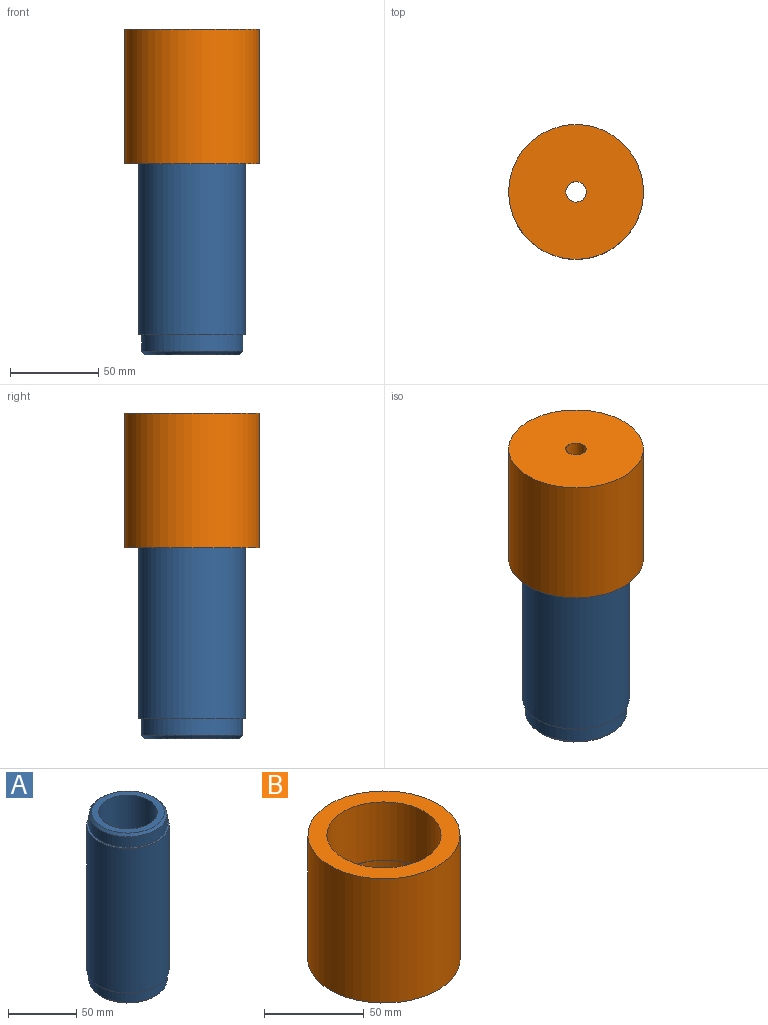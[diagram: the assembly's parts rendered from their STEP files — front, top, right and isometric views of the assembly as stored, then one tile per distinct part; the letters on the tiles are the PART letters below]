
ASSEMBLY  parts=2 mates=1
PART A: 10 faces, bbox 60.3x60.3x152.4 mm
  f0: cylinder r=30.16mm len=129.54mm, axis (0,0,-1), area 24550mm2, adj f1,f9
  f1: plane 60.33x60.33mm, normal (0,0,-1), area 292.9mm2, adj f0,f2
  f2: cylinder r=28.57mm len=57.15mm, axis (0,0,-1), area 1710.1mm2, adj f1,f3
  f3: cone r=28.57mm half-angle=45deg, axis (0,0,1), area 467.6mm2, adj f2,f4
  f4: plane 53.34x53.34mm, normal (0,0,-1), area 792.5mm2, adj f3,f5
  f5: cylinder r=21.42mm len=152.4mm, axis (0,0,-1), area 20515.6mm2, adj f4,f6
  f6: plane 53.34x53.34mm, normal (0,0,1), area 792.5mm2, adj f5,f7
  f7: cone r=28.57mm half-angle=45deg, axis (0,0,-1), area 467.6mm2, adj f6,f8
  f8: cylinder r=28.57mm len=57.15mm, axis (0,0,-1), area 1710.1mm2, adj f7,f9
  f9: plane 60.33x60.33mm, normal (0,0,1), area 292.9mm2, adj f0,f8
PART B: 14 faces, bbox 76.2x76.2x76.2 mm
  f0: torus R=29.59mm, axis (0,0,-1), area 74.6mm2, adj f1,f12
  f1: plane 59.18x59.18mm, normal (0,0,-1), area 158.2mm2, adj f0,f2
  f2: torus R=28.73mm, axis (0,0,-1), area 35.9mm2, adj f1,f3
  f3: cylinder r=28.6mm len=57.2mm, axis (0,0,-1), area 6424.4mm2, adj f2,f4
  f4: plane 76.2x76.2mm, normal (0,0,1), area 1990.6mm2, adj f3,f5
  f5: cylinder r=38.1mm len=76.2mm, axis (0,0,-1), area 18241.5mm2, adj f4,f6
  f6: plane 76.2x76.2mm, normal (0,0,-1), area 4456.3mm2, adj f5,f13
  f7: plane 57.2x57.2mm, normal (0,0,1), area 2465.7mm2, adj f8,f13
  f8: cylinder r=28.6mm len=57.2mm, axis (0,0,-1), area 570.6mm2, adj f7,f9
  f9: torus R=28.73mm, axis (0,0,-1), area 35.9mm2, adj f8,f10
  f10: plane 59.18x59.18mm, normal (0,0,1), area 158.2mm2, adj f9,f11
  f11: torus R=29.59mm, axis (0,0,-1), area 74.6mm2, adj f10,f12
  f12: cylinder r=29.84mm len=59.69mm, axis (0,0,-1), area 893.1mm2, adj f0,f11
  f13: cylinder r=5.75mm len=31.75mm, axis (0,0,-1), area 1147.9mm2, adj f6,f7
PLACE A t=(-27.38,-8.54,4.6)mm
PLACE B rot(axis=(1,0,0),180deg) t=(-27.38,-8.54,112.55)mm
MATE cylindrical B.f0 <-> A.f0  axis (0,0,-1) through (-27.38,-8.54,80.8)mm
